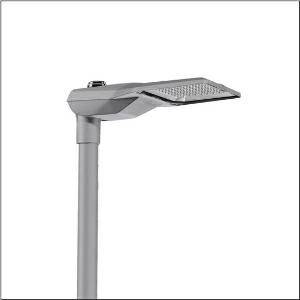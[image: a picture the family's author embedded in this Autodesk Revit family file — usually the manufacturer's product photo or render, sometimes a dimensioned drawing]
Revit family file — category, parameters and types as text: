
# Revit family: streetlight_sl_21_midi___st1_5a_5xe7p47n08mb_d352
name_source: partatom
category: Lighting Fixtures
units: mm (PartAtom-declared; Revit-internal decimal feet)

## family parameters
Cut with Voids When Loaded = No
Host = Face
Light Source = No
Part Type = Normal
Room Calculation Point = No
Round Connector Dimension = Use Diameter
Shared = No

## types (1)
- --- (1 x LED, 19830 lm, 147 W, 4000K)
    Apparent Load = 147 VA
    CIE Flux Codes = 22 53 95 100 100
    Color Rendering = 70
    Color Temperature = 4000K
    Default Elevation = 1800 mm
    Description = Streetlight SL 21 midi, mast luminaire, primary light control with lens, of PMMA, primary optical cover: cover, of toughened safety glass, transparent, light distribution: ST1.5a, light emission: direct distribution, primary light characteristic: asymmetric, installation type: side-entry, LED, 3G 2.5mm², High Power LED, rated luminous flux: 19.830lm, luminous efficacy: 135lm/W, light colour: 740, colour temperature: 4000K, control: overheat protection, presetting dimming linear, constant luminous flux control, time-dependent luminous flux control, flexible luminous flux parameterisation, mains connection: 220..240V, AC, 50/60Hz, connection cable pre-assembled, cable length: 12,5m, wiring characteristics: H05VV-F, start of lifetime: 147W, end of service life: 155W, reduction: 65W, luminaire housing, of diecast aluminium (EN AC-44300), powder-coated, Siteco® metallic grey (DB 702S), corrosivity category C5 mid according to DIN EN ISO 12944, multi-level sealing system, sealing non-destructively replaceable, inclination adjustable: 0°, 5°, 10°, 15°, length: 644mm, width: 335mm, height: 110mm, spigot size: 42mm (side-entry), protection rating (complete): IP66, insulation class (complete): insulation class I (protective earthing), certification: CE, ENEC, ENEC+, VDE, impact resistance: IK09, permissible operating ambient temperature for outdoor applications: -40..+50°C, standard-compliant lighting for roads and squares, packaging unit: 1 piece

Light Distribution: ST1.5a
    Height = 111 mm
    Lamp = 1 x LED
    Lamp Light Flux = 19830 lm
    Lamp Power = 147 W
    Lamp count = 1
    Length = 644 mm
    Luminous efficacy = 135 lm/W
    Manufacturer = Siteco
    ModVariant = No
    Model = 5XE7P47N08MB
    Number of Poles = 1
    OnlyDefault = Yes
    Power Factor = 1
    Product Name = Streetlight SL 21 midi | ST1.5a
    Product group = mast luminaire | pylon top
    ProductGroupID = 6100
    Protection Class = Protection class I
    Protection Degree = IP 66
    RLX_Detail_Level = 1
    RLX_Emergency_Light_Flux = 0 lm
    RLX_Emergency_Type = 0
    RLX_Emergency_Type_DB = No
    RlxData = <blob elided: 95073 chars, md5=c56e0c39>
    Socket = socket
    Standby Power = 0 W
    System Light Flux = 19830 lm
    System Power = 147 W
    Type Comments = factory setting: luminous flux: 100 % | dim-lin: 254 | 750 mA
    Type Image = l_1294377.jpg
    URL = http://relux.com
    VarID = @adj_082761
    Voltage = 0 V
    Weight = 0.00 kg
    Width = 336 mm

## geometry (parser evidence)
native form markers: Blend x4, Sweep x10
no freeform markers — native parametric forms only
